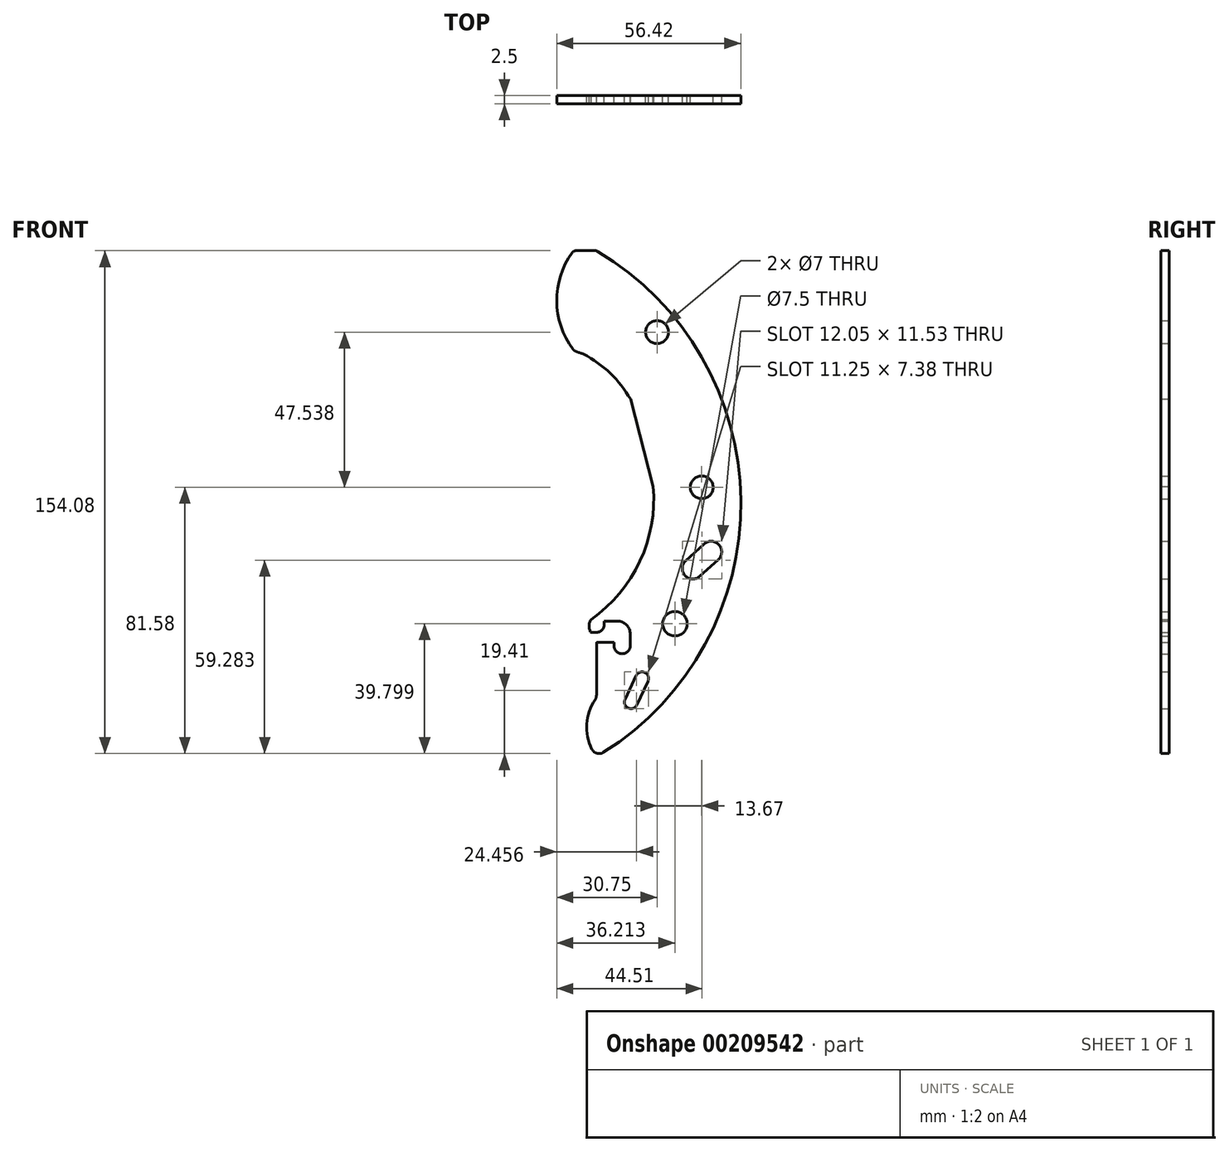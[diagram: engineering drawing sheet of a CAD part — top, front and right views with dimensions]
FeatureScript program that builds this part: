
annotation { "Feature Type Name" : "Feature", "Feature Type Description" : "" }
export const myFeature = defineFeature(function(context is Context, id is Id, definition is map)
    precondition{}
    {
        {
            var Q0;
            Q0=qCreatedBy(makeId("Front.planeOp"),FACE);
            var sketch = newSketch(context, id + "F0", { "sketchPlane" : qUnion([Q0])});
            skArc(sketch, "E0", {"start": v(47.9, -76.2) * mm, "mid": v(90, 1.05) * mm, "end": v(46.11, 77.29) * mm});
            skLineSegment(sketch, "E1", {"start": v(45.76, 77.5) * mm, "end": v(45.76, -77.5) * mm, "construction": true});
            skLineSegment(sketch, "E2", {"start": v(0, 0) * mm, "end": v(90, 0) * mm, "construction": true});
            skLineSegment(sketch, "E3", {"start": v(0, 5) * mm, "end": v(20, 5) * mm, "construction": true});
            skLineSegment(sketch, "E4", {"start": v(20, 5) * mm, "end": v(18.3, 1.37) * mm, "construction": true});
            skLineSegment(sketch, "E5", {"start": v(20, 5) * mm, "end": v(20, -95) * mm, "construction": true});
            skPoint(sketch, "E6", {"position": v(18.3, 1.37) * mm});
            skArc(sketch, "E7", {"start": v(18.3, -43.63) * mm, "mid": v(19.15, -43.62) * mm, "end": v(20, -43.6) * mm, "construction": true});
            skLineSegment(sketch, "E8", {"start": v(18.3, 1.37) * mm, "end": v(18.3, -98.63) * mm, "construction": true});
            skLineSegment(sketch, "E9", {"start": v(18.3, 1.37) * mm, "end": v(44.12, -35.49) * mm, "construction": true});
            skLineSegment(sketch, "E10", {"start": v(18.3, 1.37) * mm, "end": v(63.14, 5.3) * mm, "construction": true});
            skLineSegment(sketch, "E11", {"start": v(20, 5) * mm, "end": v(120, 5) * mm, "construction": true});
            skLineSegment(sketch, "E12", {"start": v(20, 5) * mm, "end": v(69.8, -36.78) * mm, "construction": true});
            skPoint(sketch, "E13", {"position": v(69.8, -36.78) * mm});
            skPoint(sketch, "E14", {"position": v(78, 5) * mm});
            skArc(sketch, "E15.trimOffspring", {"start": v(44.12, -35.49) * mm, "mid": v(59.1, -17.64) * mm, "end": v(63.14, 5.3) * mm});
            skLineSegment(sketch, "E16", {"start": v(20, 5) * mm, "end": v(64.33, 52.54) * mm, "construction": true});
            skPoint(sketch, "E17", {"position": v(64.33, 52.54) * mm});
            skLineSegment(sketch, "E18", {"start": v(20, 5) * mm, "end": v(80.87, -14.78) * mm, "construction": true});
            skArc(sketch, "E19", {"start": v(83.05, -17.18) * mm, "mid": v(83.27, -12.6) * mm, "end": v(78.68, -12.37) * mm});
            skPoint(sketch, "E20", {"position": v(20, -70) * mm});
            skLineSegment(sketch, "E21", {"start": v(20, -70) * mm, "end": v(80.87, -14.78) * mm, "construction": true});
            skPoint(sketch, "E22", {"position": v(75.31, -19.82) * mm});
            skArc(sketch, "E23", {"start": v(73.13, -17.4) * mm, "mid": v(72.9, -22) * mm, "end": v(77.5, -22.22) * mm});
            skLineSegment(sketch, "E24", {"start": v(77.5, -22.22) * mm, "end": v(83.05, -17.18) * mm});
            skLineSegment(sketch, "E25", {"start": v(73.13, -17.4) * mm, "end": v(78.68, -12.37) * mm});
            skLineSegment(sketch, "E26", {"start": v(20, -70) * mm, "end": v(59.73, -53.54) * mm, "construction": true});
            skLineSegment(sketch, "E27", {"start": v(59.73, -53.54) * mm, "end": v(56.35, -60.8) * mm, "construction": true});
            skArc(sketch, "E28", {"start": v(54.53, -59.95) * mm, "mid": v(55.5, -62.6) * mm, "end": v(58.16, -61.64) * mm});
            skArc(sketch, "E29", {"start": v(61.54, -54.39) * mm, "mid": v(60.57, -51.73) * mm, "end": v(57.91, -52.7) * mm});
            skLineSegment(sketch, "E30", {"start": v(61.54, -54.39) * mm, "end": v(58.16, -61.64) * mm});
            skPoint(sketch, "E30.endSnap0", {"position": v(58.04, -57.17) * mm});
            skLineSegment(sketch, "E31", {"start": v(57.91, -52.7) * mm, "end": v(54.53, -59.95) * mm});
            skPoint(sketch, "E32.orphan", {"position": v(58.04, -61.9) * mm});
            skLineSegment(sketch, "E33", {"start": v(20, 5) * mm, "end": v(20, 105) * mm, "construction": true});
            skLineSegment(sketch, "E34", {"start": v(20, 5) * mm, "end": v(44.51, 57.57) * mm, "construction": true});
            skArc(sketch, "E35", {"start": v(39.07, 46.87) * mm, "mid": v(40.27, 46.34) * mm, "end": v(41.5, 45.95) * mm});
            skPoint(sketch, "E36", {"position": v(20, 14) * mm});
            skLineSegment(sketch, "E37", {"start": v(20, 14) * mm, "end": v(25, 14) * mm, "construction": true});
            skPoint(sketch, "E38", {"position": v(25, 14) * mm});
            skArc(sketch, "E39", {"start": v(25, 50) * mm, "mid": v(22.5, 49.91) * mm, "end": v(20, 49.65) * mm, "construction": true});
            skLineSegment(sketch, "E40", {"start": v(25, 14) * mm, "end": v(56.18, 32) * mm, "construction": true});
            skLineSegment(sketch, "E41", {"start": v(25, 14) * mm, "end": v(40.21, 46.63) * mm, "construction": true});
            skLineSegment(sketch, "E42", {"start": v(25, 14) * mm, "end": v(25, 55) * mm, "construction": true});
            skPoint(sketch, "E42.endSnap0", {"position": v(20, 55) * mm});
            skArc(sketch, "E43.trimOffspring", {"start": v(56.18, 32) * mm, "mid": v(49.98, 39.92) * mm, "end": v(41.83, 45.82) * mm});
            skLineSegment(sketch, "E44", {"start": v(45.35, 77.5) * mm, "end": v(39.51, 77.5) * mm});
            skArc(sketch, "E45", {"start": v(38.3, 76.88) * mm, "mid": v(33.58, 62.05) * mm, "end": v(38.55, 47.3) * mm});
            skPoint(sketch, "E46.visualSharp", {"position": v(38.76, 77.5) * mm});
            skArc(sketch, "E46.filletArc", {"start": v(39.51, 77.5) * mm, "mid": v(38.83, 77.34) * mm, "end": v(38.3, 76.88) * mm});
            skPoint(sketch, "E47.visualSharp", {"position": v(45.76, 77.5) * mm});
            skArc(sketch, "E47.filletArc", {"start": v(46.11, 77.29) * mm, "mid": v(45.74, 77.45) * mm, "end": v(45.35, 77.5) * mm});
            skPoint(sketch, "E48.visualSharp", {"position": v(38.76, 47.04) * mm});
            skArc(sketch, "E48.filletArc", {"start": v(38.55, 47.3) * mm, "mid": v(38.79, 47.06) * mm, "end": v(39.07, 46.87) * mm});
            skPoint(sketch, "E49.visualSharp", {"position": v(41.67, 45.9) * mm});
            skArc(sketch, "E49.filletArc", {"start": v(41.83, 45.82) * mm, "mid": v(41.68, 45.9) * mm, "end": v(41.5, 45.95) * mm});
            skLineSegment(sketch, "E50", {"start": v(56.18, 32) * mm, "end": v(63.14, 5.3) * mm});
            skPoint(sketch, "E51", {"position": v(45.76, -59.5) * mm});
            skArc(sketch, "E52", {"start": v(45.33, -60.1) * mm, "mid": v(42.8, -67.51) * mm, "end": v(44.33, -75.2) * mm});
            skPoint(sketch, "E53", {"position": v(44.12, -39.49) * mm});
            skLineSegment(sketch, "E54", {"start": v(44.12, -39.49) * mm, "end": v(45.62, -39.49) * mm});
            skLineSegment(sketch, "E55", {"start": v(48.12, -36.99) * mm, "end": v(48.12, -35.99) * mm});
            skLineSegment(sketch, "E56", {"start": v(48.12, -35.99) * mm, "end": v(52.12, -35.99) * mm});
            skLineSegment(sketch, "E57", {"start": v(56.12, -39.99) * mm, "end": v(56.12, -43.49) * mm});
            skLineSegment(sketch, "E58", {"start": v(53.62, -45.99) * mm, "end": v(53.62, -45.99) * mm});
            skLineSegment(sketch, "E59", {"start": v(51.12, -43.49) * mm, "end": v(51.12, -42.49) * mm});
            skLineSegment(sketch, "E60", {"start": v(51.12, -42.49) * mm, "end": v(46, -42.49) * mm});
            skLineSegment(sketch, "E61", {"start": v(45.76, -42.74) * mm, "end": v(45.76, -58.7) * mm});
            skPoint(sketch, "E62.visualSharp", {"position": v(56.12, -35.99) * mm});
            skArc(sketch, "E62.filletArc", {"start": v(56.12, -39.99) * mm, "mid": v(54.95, -37.16) * mm, "end": v(52.12, -35.99) * mm});
            skPoint(sketch, "E63.visualSharp", {"position": v(56.12, -45.99) * mm});
            skArc(sketch, "E63.filletArc", {"start": v(53.62, -45.99) * mm, "mid": v(55.39, -45.25) * mm, "end": v(56.12, -43.49) * mm});
            skPoint(sketch, "E64.visualSharp", {"position": v(51.12, -45.99) * mm});
            skArc(sketch, "E64.filletArc", {"start": v(51.12, -43.49) * mm, "mid": v(51.85, -45.25) * mm, "end": v(53.62, -45.99) * mm});
            skArc(sketch, "E65", {"start": v(44.12, -35.49) * mm, "mid": v(43.5, -37.49) * mm, "end": v(44.12, -39.49) * mm});
            skPoint(sketch, "E66.visualSharp", {"position": v(48.12, -39.49) * mm});
            skArc(sketch, "E66.filletArc", {"start": v(45.62, -39.49) * mm, "mid": v(47.39, -38.75) * mm, "end": v(48.12, -36.99) * mm});
            skPoint(sketch, "E67.visualSharp", {"position": v(45.76, -77.5) * mm});
            skArc(sketch, "E67.filletArc", {"start": v(44.33, -75.2) * mm, "mid": v(45.9, -76.48) * mm, "end": v(47.9, -76.2) * mm});
            skArc(sketch, "E68.filletArc", {"start": v(45.33, -60.1) * mm, "mid": v(45.65, -59.43) * mm, "end": v(45.76, -58.7) * mm});
            skPoint(sketch, "E69.visualSharp", {"position": v(45.76, -42.49) * mm});
            skArc(sketch, "E69.filletArc", {"start": v(46, -42.49) * mm, "mid": v(45.83, -42.56) * mm, "end": v(45.76, -42.74) * mm});
            skSolve(sketch);
        }
        {
            var Q0;
            Q0=makeQuery(id+"F0.imprint","IMPRINT",FACE,{"disambiguationData":[TD([[makeQuery(id+"F0.imprint","IMPRINT",EDGE,{"derivedFrom":sQuery(id+"F0.wireOp",EDGE,"E0")}),1.0]])]});
            extrude(context, id + "F1", {"entities" : qUnion([Q0]), "depth" : 2.5 * mm});
        }
        {
            var Q0;
            Q0=sQuery(id+"F0.wireOp",VERTEX,"E17");
            var Q1;
            Q1=sQuery(id+"F0.wireOp",VERTEX,"E14");
            var Q2;
            Q2=makeQuery(id+"F1.opExtrude","SWEPT_BODY",BODY,{"disambiguationData":[OSD([sQuery(id+"F0.wireOp",EDGE,"E0"),sQuery(id+"F0.wireOp",EDGE,"E15.trimOffspring"),sQuery(id+"F0.wireOp",EDGE,"E19"),sQuery(id+"F0.wireOp",EDGE,"E23"),sQuery(id+"F0.wireOp",EDGE,"E24"),sQuery(id+"F0.wireOp",EDGE,"E25"),sQuery(id+"F0.wireOp",EDGE,"E28"),sQuery(id+"F0.wireOp",EDGE,"E29"),sQuery(id+"F0.wireOp",EDGE,"E30"),sQuery(id+"F0.wireOp",EDGE,"E31"),sQuery(id+"F0.wireOp",EDGE,"E35"),sQuery(id+"F0.wireOp",EDGE,"E43.trimOffspring"),sQuery(id+"F0.wireOp",EDGE,"E44"),sQuery(id+"F0.wireOp",EDGE,"E45"),sQuery(id+"F0.wireOp",EDGE,"E46.filletArc"),sQuery(id+"F0.wireOp",EDGE,"E47.filletArc"),sQuery(id+"F0.wireOp",EDGE,"E48.filletArc"),sQuery(id+"F0.wireOp",EDGE,"E49.filletArc"),sQuery(id+"F0.wireOp",EDGE,"E50"),sQuery(id+"F0.wireOp",EDGE,"E52"),sQuery(id+"F0.wireOp",EDGE,"E54"),sQuery(id+"F0.wireOp",EDGE,"E55"),sQuery(id+"F0.wireOp",EDGE,"E56"),sQuery(id+"F0.wireOp",EDGE,"E57"),sQuery(id+"F0.wireOp",EDGE,"E59"),sQuery(id+"F0.wireOp",EDGE,"E60"),sQuery(id+"F0.wireOp",EDGE,"E61"),sQuery(id+"F0.wireOp",EDGE,"E62.filletArc"),sQuery(id+"F0.wireOp",EDGE,"E63.filletArc"),sQuery(id+"F0.wireOp",EDGE,"E64.filletArc"),sQuery(id+"F0.wireOp",EDGE,"E65"),sQuery(id+"F0.wireOp",EDGE,"E66.filletArc"),sQuery(id+"F0.wireOp",EDGE,"E67.filletArc"),sQuery(id+"F0.wireOp",EDGE,"E68.filletArc"),sQuery(id+"F0.wireOp",EDGE,"E69.filletArc")])]});
            hole(context, id + "F2", {"style" : HoleStyle.SIMPLE, "endStyle" : HoleEndStyle.THROUGH, "oppositeDirection" : true, "holeDiameter" : 7 * mm, "locations" : qUnion([Q0, Q1]), "scope" : qUnion([Q2]), "isTappedThrough" : true});
        }
        {
            var Q0;
            Q0=sQuery(id+"F0.wireOp",VERTEX,"E13");
            var Q1;
            Q1=makeQuery(id+"F1.opExtrude","SWEPT_BODY",BODY,{"disambiguationData":[OSD([sQuery(id+"F0.wireOp",EDGE,"E0"),sQuery(id+"F0.wireOp",EDGE,"E15.trimOffspring"),sQuery(id+"F0.wireOp",EDGE,"E19"),sQuery(id+"F0.wireOp",EDGE,"E23"),sQuery(id+"F0.wireOp",EDGE,"E24"),sQuery(id+"F0.wireOp",EDGE,"E25"),sQuery(id+"F0.wireOp",EDGE,"E28"),sQuery(id+"F0.wireOp",EDGE,"E29"),sQuery(id+"F0.wireOp",EDGE,"E30"),sQuery(id+"F0.wireOp",EDGE,"E31"),sQuery(id+"F0.wireOp",EDGE,"E35"),sQuery(id+"F0.wireOp",EDGE,"E43.trimOffspring"),sQuery(id+"F0.wireOp",EDGE,"E44"),sQuery(id+"F0.wireOp",EDGE,"E45"),sQuery(id+"F0.wireOp",EDGE,"E46.filletArc"),sQuery(id+"F0.wireOp",EDGE,"E47.filletArc"),sQuery(id+"F0.wireOp",EDGE,"E48.filletArc"),sQuery(id+"F0.wireOp",EDGE,"E49.filletArc"),sQuery(id+"F0.wireOp",EDGE,"E50"),sQuery(id+"F0.wireOp",EDGE,"E52"),sQuery(id+"F0.wireOp",EDGE,"E54"),sQuery(id+"F0.wireOp",EDGE,"E55"),sQuery(id+"F0.wireOp",EDGE,"E56"),sQuery(id+"F0.wireOp",EDGE,"E57"),sQuery(id+"F0.wireOp",EDGE,"E59"),sQuery(id+"F0.wireOp",EDGE,"E60"),sQuery(id+"F0.wireOp",EDGE,"E61"),sQuery(id+"F0.wireOp",EDGE,"E62.filletArc"),sQuery(id+"F0.wireOp",EDGE,"E63.filletArc"),sQuery(id+"F0.wireOp",EDGE,"E64.filletArc"),sQuery(id+"F0.wireOp",EDGE,"E65"),sQuery(id+"F0.wireOp",EDGE,"E66.filletArc"),sQuery(id+"F0.wireOp",EDGE,"E67.filletArc"),sQuery(id+"F0.wireOp",EDGE,"E68.filletArc"),sQuery(id+"F0.wireOp",EDGE,"E69.filletArc")])]});
            hole(context, id + "F3", {"style" : HoleStyle.SIMPLE, "endStyle" : HoleEndStyle.THROUGH, "oppositeDirection" : true, "holeDiameter" : 7.5 * mm, "locations" : qUnion([Q0]), "scope" : qUnion([Q1]), "isTappedThrough" : true});
        }
    });
